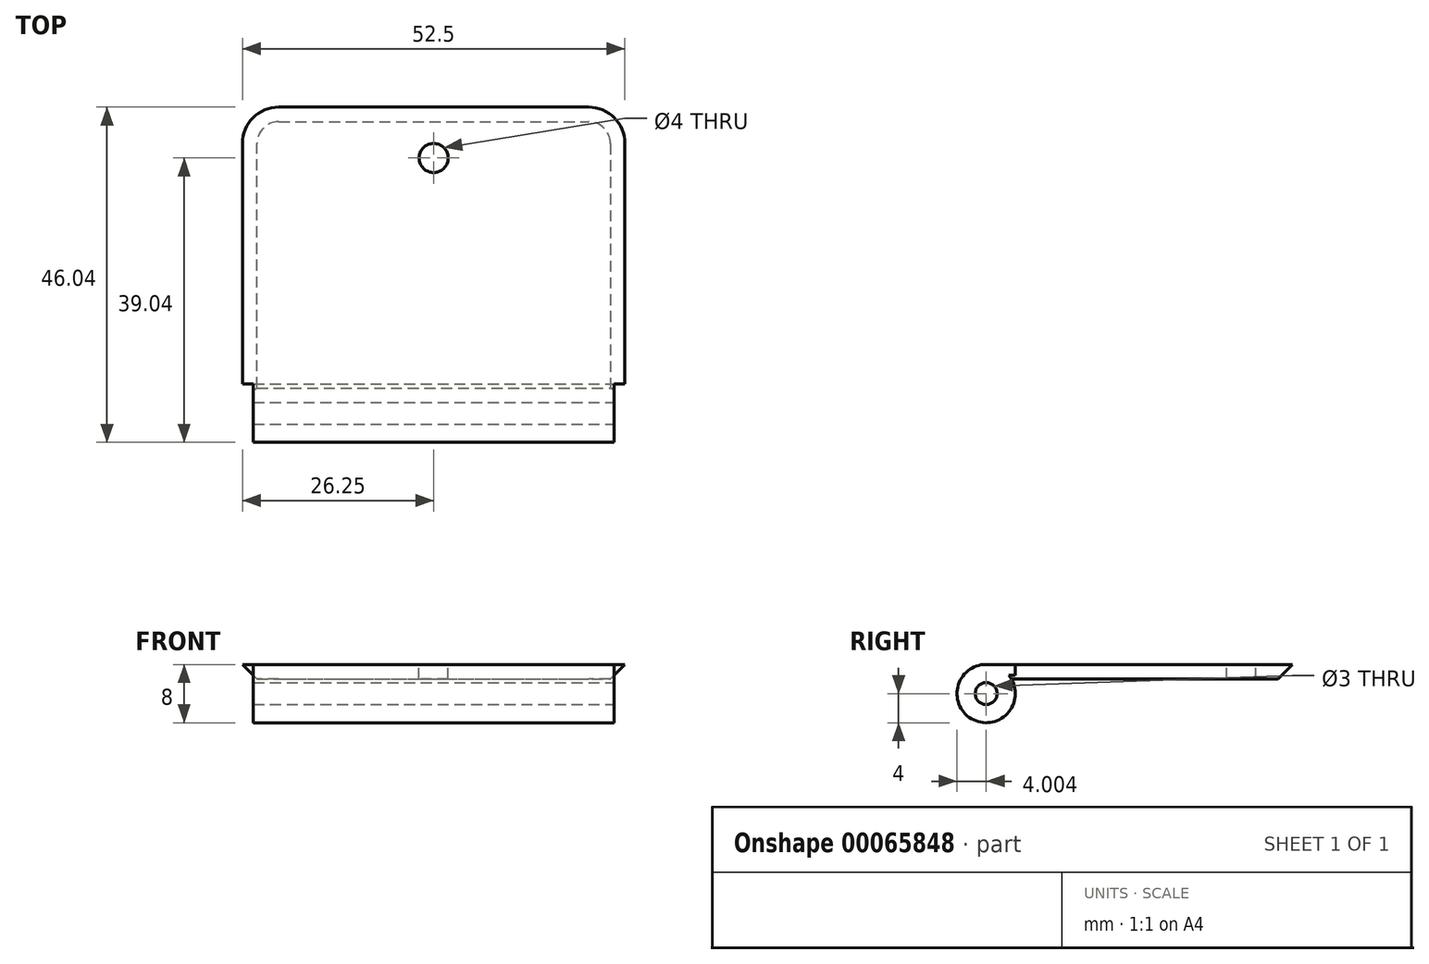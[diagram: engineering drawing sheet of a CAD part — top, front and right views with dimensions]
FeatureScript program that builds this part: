
annotation { "Feature Type Name" : "Feature", "Feature Type Description" : "" }
export const myFeature = defineFeature(function(context is Context, id is Id, definition is map)
    precondition{}
    {
        {
            var Q0;
            Q0=qCreatedBy(makeId("Top.planeOp"),FACE);
            var sketch = newSketch(context, id + "F0", { "sketchPlane" : qUnion([Q0])});
            skLineSegment(sketch, "E0.bottom", {"start": v(26.25, -22.75) * mm, "end": v(-26.25, -22.75) * mm});
            skLineSegment(sketch, "E0.top", {"start": v(26.25, 22.75) * mm, "end": v(-26.25, 22.75) * mm});
            skLineSegment(sketch, "E0.left", {"start": v(26.25, -22.75) * mm, "end": v(26.25, 22.75) * mm});
            skLineSegment(sketch, "E0.right", {"start": v(-26.25, -22.75) * mm, "end": v(-26.25, 22.75) * mm});
            skPoint(sketch, "E0.middle", {"position": v(0, 0) * mm});
            skSolve(sketch);
        }
        {
            var Q0;
            Q0 = qSketchRegion(id + "F0", true);
            extrude(context, id + "F1", {"entities" : qUnion([Q0]), "depth" : 2 * mm});
        }
        {
            var Q0;
            Q0=makeQuery(id+"F1.opExtrude","SWEPT_FACE",FACE,{"disambiguationData":[OSD([sQuery(id+"F0.wireOp",EDGE,"E0.left")])]});
            var sketch = newSketch(context, id + "F2", { "sketchPlane" : qUnion([Q0])});
            skCircle(sketch, "E1", {"center": v(-19.29, -2) * mm, "radius": 4 * mm});
            skCircle(sketch, "E2", {"center": v(-19.29, -2) * mm, "radius": 1.5 * mm});
            skSolve(sketch);
        }
        {
            var Q0;
            Q0 = qSketchRegion(id + "F2", true);
            var Q1;
            Q1=makeQuery(id+"F2.imprint","IMPRINT",FACE,{"disambiguationData":[TD([[makeQuery(id+"F2.imprint","IMPRINT",EDGE,{"derivedFrom":sQuery(id+"F2.wireOp",EDGE,"E2")}),-1.0]])]});
            var Q2;
            Q2=makeQuery(id+"F1.opExtrude","SWEPT_FACE",FACE,{"disambiguationData":[OSD([sQuery(id+"F0.wireOp",EDGE,"E0.right")])]});
            extrude(context, id + "F3", {"entities" : qUnion([Q0, Q1]), "operationType" : NewBodyOperationType.ADD, "endBound" : BoundingType.UP_TO_SURFACE, "oppositeDirection" : true, "endBoundEntityFace" : qUnion([Q2]), "depth" : 25 * mm});
        }
        {
            var Q0;
            Q0=makeQuery(id+"F1.opExtrude","SWEPT_EDGE",EDGE,{"disambiguationData":[OSD([sQuery(id+"F0.wireOp",EDGE,"E0.top"),sQuery(id+"F0.wireOp",EDGE,"E0.left")])]});
            var Q1;
            Q1=makeQuery(id+"F1.opExtrude","SWEPT_EDGE",EDGE,{"disambiguationData":[OSD([sQuery(id+"F0.wireOp",EDGE,"E0.top"),sQuery(id+"F0.wireOp",EDGE,"E0.right")])]});
            fillet(context, id + "F4", {"entities" : qUnion([Q0, Q1]), "radius" : 5 * mm, "tangentPropagation" : true, "allowEdgeOverflow" : false});
        }
        {
            var Q0;
            Q0=makeQuery(id+"F1.opExtrude","CAP_EDGE",EDGE,{"disambiguationData":[OSD([sQuery(id+"F0.wireOp",EDGE,"E0.right")])],"isStart":true});
            var Q1;
            {var subQ0=sQuery(id+"F0.wireOp",EDGE,"E0.right");var subQ1=sQuery(id+"F0.wireOp",EDGE,"E0.top");Q1=makeQuery(id+"F4.opFillet","BLEND_EDGE",EDGE,{"blendedFrom":[makeQuery(id+"F1.opExtrude","SWEPT_EDGE",EDGE,{"disambiguationData":[OSD([subQ1,subQ0])]}),makeQuery(id+"F1.opExtrude","CAP_FACE",FACE,{"disambiguationData":[OSD([sQuery(id+"F0.wireOp",EDGE,"E0.bottom"),subQ1,sQuery(id+"F0.wireOp",EDGE,"E0.left"),subQ0])],"isStart":true})],"blendedInto":[makeQuery(id+"F1.opExtrude","CAP_FACE",FACE,{"disambiguationData":[OSD([sQuery(id+"F0.wireOp",EDGE,"E0.bottom"),subQ1,sQuery(id+"F0.wireOp",EDGE,"E0.left"),subQ0])],"isStart":true})]});}
            var Q2;
            Q2=makeQuery(id+"F1.opExtrude","CAP_EDGE",EDGE,{"disambiguationData":[OSD([sQuery(id+"F0.wireOp",EDGE,"E0.top")])],"isStart":true});
            var Q3;
            {var subQ0=sQuery(id+"F0.wireOp",EDGE,"E0.left");var subQ1=sQuery(id+"F0.wireOp",EDGE,"E0.top");Q3=makeQuery(id+"F4.opFillet","BLEND_EDGE",EDGE,{"blendedFrom":[makeQuery(id+"F1.opExtrude","SWEPT_EDGE",EDGE,{"disambiguationData":[OSD([subQ1,subQ0])]}),makeQuery(id+"F1.opExtrude","CAP_FACE",FACE,{"disambiguationData":[OSD([sQuery(id+"F0.wireOp",EDGE,"E0.bottom"),subQ1,subQ0,sQuery(id+"F0.wireOp",EDGE,"E0.right")])],"isStart":true})],"blendedInto":[makeQuery(id+"F1.opExtrude","CAP_FACE",FACE,{"disambiguationData":[OSD([sQuery(id+"F0.wireOp",EDGE,"E0.bottom"),subQ1,subQ0,sQuery(id+"F0.wireOp",EDGE,"E0.right")])],"isStart":true})]});}
            var Q4;
            Q4=makeQuery(id+"F1.opExtrude","CAP_EDGE",EDGE,{"disambiguationData":[OSD([sQuery(id+"F0.wireOp",EDGE,"E0.left")])],"isStart":true});
            chamfer(context, id + "F5", {"entities" : qUnion([Q0, Q1, Q2, Q3, Q4]), "width" : 2 * mm, "tangentPropagation" : true});
        }
        {
            var Q0;
            Q0=makeQuery(id+"F1.opExtrude","CAP_FACE",FACE,{"disambiguationData":[OSD([sQuery(id+"F0.wireOp",EDGE,"E0.bottom"),sQuery(id+"F0.wireOp",EDGE,"E0.top"),sQuery(id+"F0.wireOp",EDGE,"E0.left"),sQuery(id+"F0.wireOp",EDGE,"E0.right")])],"isStart":false});
            var sketch = newSketch(context, id + "F6", { "sketchPlane" : qUnion([Q0])});
            skCircle(sketch, "E3", {"center": v(0, 15.75) * mm, "radius": 2 * mm});
            skSolve(sketch);
        }
        {
            var Q0;
            Q0 = qSketchRegion(id + "F6", true);
            extrude(context, id + "F7", {"entities" : qUnion([Q0]), "operationType" : NewBodyOperationType.REMOVE, "oppositeDirection" : true, "depth" : 25 * mm});
        }
        {
            var Q0;
            Q0=makeQuery(id+"F1.opExtrude","SWEPT_FACE",FACE,{"disambiguationData":[OSD([sQuery(id+"F0.wireOp",EDGE,"E0.right")])]});
            var sketch = newSketch(context, id + "F8", { "sketchPlane" : qUnion([Q0])});
            skCircle(sketch, "E4", {"center": v(-19.34, -2) * mm, "radius": 4 * mm});
            skCircle(sketch, "E5", {"center": v(-19.34, -2) * mm, "radius": 1.5 * mm});
            skSolve(sketch);
        }
        {
            var Q0;
            {var subQ0=sQuery(id+"F0.wireOp",EDGE,"E0.right");Q0=makeQuery(id+"F8.imprint","IMPRINT",FACE,{"disambiguationData":[TD([[makeQuery(id+"F8.imprint","IMPRINT",EDGE,{"derivedFrom":makeQuery(id+"F1.opExtrude","CAP_EDGE",EDGE,{"disambiguationData":[OSD([subQ0])],"isStart":false})}),1.0]])]});}
            var sketch = newSketch(context, id + "F9", { "sketchPlane" : qUnion([Q0])});
            skCircle(sketch, "E6", {"center": v(19.29, -2) * mm, "radius": 4 * mm});
            skSolve(sketch);
        }
        {
            var Q0;
            Q0=makeQuery(id+"F9.imprint","IMPRINT",FACE,{"disambiguationData":[TD([[makeQuery(id+"F9.imprint","IMPRINT",EDGE,{"disambiguationData":[OD(0.0)],"derivedFrom":sQuery(id+"F9.wireOp",EDGE,"E6")}),-1.0]])]});
            extrude(context, id + "F10", {"entities" : qUnion([Q0]), "operationType" : NewBodyOperationType.REMOVE, "oppositeDirection" : true, "depth" : 70 * mm});
        }
        {
            var Q0;
            Q0=makeQuery(id+"F3.boolean.opBoolean","MERGE",FACE,{"derivedFrom":[makeQuery(id+"F1.opExtrude","SWEPT_FACE",FACE,{"disambiguationData":[OSD([sQuery(id+"F0.wireOp",EDGE,"E0.left")])]}),makeQuery(id+"F3.opExtrude","CAP_FACE",FACE,{"disambiguationData":[OSD([sQuery(id+"F2.wireOp",EDGE,"E1"),sQuery(id+"F2.wireOp",EDGE,"E2")])],"isStart":true})]});
            extrude(context, id + "F11", {"entities" : qUnion([Q0]), "operationType" : NewBodyOperationType.REMOVE, "oppositeDirection" : true, "depth" : 1.5 * mm});
        }
        {
            var Q0;
            {var subQ0=sQuery(id+"F0.wireOp",EDGE,"E0.right");Q0=makeQuery(id+"F8.imprint","IMPRINT",FACE,{"disambiguationData":[TD([[makeQuery(id+"F8.imprint","IMPRINT",EDGE,{"derivedFrom":makeQuery(id+"F1.opExtrude","CAP_EDGE",EDGE,{"disambiguationData":[OSD([subQ0])],"isStart":false})}),1.0]])]});}
            extrude(context, id + "F12", {"entities" : qUnion([Q0]), "operationType" : NewBodyOperationType.REMOVE, "oppositeDirection" : true, "depth" : 1.5 * mm});
        }
        {
            var Q0;
            Q0=makeQuery(id+"F6.imprint","IMPRINT",FACE,{"disambiguationData":[TD([[makeQuery(id+"F6.imprint","IMPRINT",EDGE,{"derivedFrom":sQuery(id+"F6.wireOp",EDGE,"E3")}),-1.0]])]});
            var sketch = newSketch(context, id + "F13", { "sketchPlane" : qUnion([Q0])});
            skPoint(sketch, "E7", {"position": v(26.25, -19.29) * mm});
            skLineSegment(sketch, "E8.bottom", {"start": v(26.25, -19.29) * mm, "end": v(24.75, -19.29) * mm});
            skLineSegment(sketch, "E8.top", {"start": v(26.25, -15.29) * mm, "end": v(24.75, -15.29) * mm});
            skLineSegment(sketch, "E8.left", {"start": v(26.25, -19.29) * mm, "end": v(26.25, -15.29) * mm});
            skLineSegment(sketch, "E8.right", {"start": v(24.75, -19.29) * mm, "end": v(24.75, -15.29) * mm});
            skPoint(sketch, "E9", {"position": v(-26.25, -19.29) * mm});
            skPoint(sketch, "E10", {"position": v(-24.75, -19.29) * mm});
            skLineSegment(sketch, "E11.bottom", {"start": v(-26.25, -19.29) * mm, "end": v(-24.75, -19.29) * mm});
            skLineSegment(sketch, "E11.top", {"start": v(-26.25, -19.29) * mm, "end": v(-24.75, -19.29) * mm});
            skLineSegment(sketch, "E11.left", {"start": v(-26.25, -19.29) * mm, "end": v(-26.25, -19.29) * mm});
            skLineSegment(sketch, "E11.right", {"start": v(-24.75, -19.29) * mm, "end": v(-24.75, -19.29) * mm});
            skLineSegment(sketch, "E12.top", {"start": v(-26.25, -15.29) * mm, "end": v(-24.75, -15.29) * mm});
            skLineSegment(sketch, "E12.left", {"start": v(-26.25, -19.29) * mm, "end": v(-26.25, -15.29) * mm});
            skLineSegment(sketch, "E12.right", {"start": v(-24.75, -19.29) * mm, "end": v(-24.75, -15.29) * mm});
            skSolve(sketch);
        }
        {
            var Q0;
            Q0 = qSketchRegion(id + "F13", true);
            extrude(context, id + "F14", {"entities" : qUnion([Q0]), "operationType" : NewBodyOperationType.REMOVE, "oppositeDirection" : true, "depth" : 25 * mm});
        }
    });
